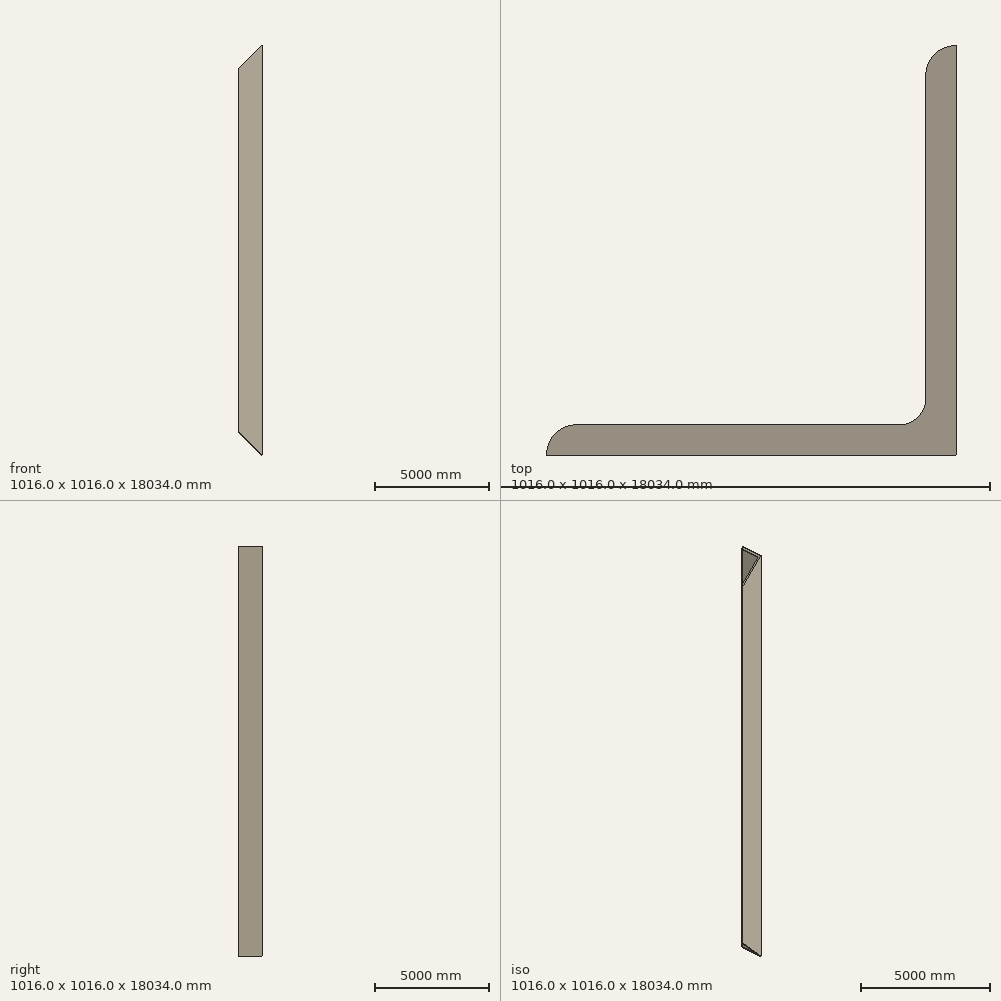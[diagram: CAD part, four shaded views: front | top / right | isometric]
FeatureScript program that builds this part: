
annotation { "Feature Type Name" : "Feature", "Feature Type Description" : "" }
export const myFeature = defineFeature(function(context is Context, id is Id, definition is map)
    precondition{}
    {
        {
            var Q0;
            Q0=qCreatedBy(makeId("Top.planeOp"),FACE);
            var sketch = newSketch(context, id + "F0", { "sketchPlane" : qUnion([Q0])});
            skLineSegment(sketch, "E0", {"start": v(0, 0) * mm, "end": v(1016, 0) * mm});
            skLineSegment(sketch, "E1", {"start": v(1016, 0) * mm, "end": v(1016, 1016) * mm});
            skLineSegment(sketch, "E2", {"start": v(939.8, 939.8) * mm, "end": v(939.8, 139.7) * mm});
            skLineSegment(sketch, "E3", {"start": v(876.3, 76.2) * mm, "end": v(76.2, 76.2) * mm});
            skPoint(sketch, "E4.visualSharp", {"position": v(939.8, 76.2) * mm});
            skArc(sketch, "E4.filletArc", {"start": v(876.3, 76.2) * mm, "mid": v(921.2, 94.8) * mm, "end": v(939.8, 139.7) * mm});
            skArc(sketch, "E5", {"start": v(76.2, 76.2) * mm, "mid": v(22.32, 53.88) * mm, "end": v(0, 0) * mm});
            skArc(sketch, "E6", {"start": v(939.8, 939.8) * mm, "mid": v(962.12, 993.68) * mm, "end": v(1016, 1016) * mm});
            skSolve(sketch);
        }
        {
            var Q0;
            Q0=makeQuery(id+"F0.imprint","IMPRINT",FACE,{"disambiguationData":[TD([[makeQuery(id+"F0.imprint","IMPRINT",EDGE,{"derivedFrom":sQuery(id+"F0.wireOp",EDGE,"E0")}),1.0]])]});
            extrude(context, id + "F1", {"entities" : qUnion([Q0]), "depth" : 18034 * mm, "offsetDistance" : 25.4 * mm});
        }
        {
            var Q0;
            Q0=makeQuery(id+"F1.opExtrude","SWEPT_FACE",FACE,{"disambiguationData":[OSD([sQuery(id+"F0.wireOp",EDGE,"E0")])]});
            var sketch = newSketch(context, id + "F2", { "sketchPlane" : qUnion([Q0])});
            skLineSegment(sketch, "E7", {"start": v(1016, 18034) * mm, "end": v(-252.04, 16765.96) * mm});
            skLineSegment(sketch, "E8", {"start": v(-252.04, 16765.96) * mm, "end": v(-252.04, 18313.7) * mm});
            skLineSegment(sketch, "E9", {"start": v(-252.04, 18313.7) * mm, "end": v(1016, 18034) * mm});
            skLineSegment(sketch, "E10", {"start": v(1016, 0) * mm, "end": v(-141.3, 1157.3) * mm});
            skLineSegment(sketch, "E11", {"start": v(-141.3, 1157.3) * mm, "end": v(-393.16, -344.64) * mm});
            skLineSegment(sketch, "E12", {"start": v(-393.16, -344.64) * mm, "end": v(1016, 0) * mm});
            skSolve(sketch);
        }
        {
            var Q0;
            Q0 = qSketchRegion(id + "F2", true);
            extrude(context, id + "F3", {"entities" : qUnion([Q0]), "operationType" : NewBodyOperationType.REMOVE, "endBound" : BoundingType.THROUGH_ALL, "oppositeDirection" : true, "depth" : 25.4 * mm, "offsetDistance" : 25.4 * mm});
        }
    });
